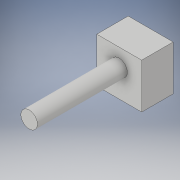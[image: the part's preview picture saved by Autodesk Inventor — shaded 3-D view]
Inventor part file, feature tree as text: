
AUTODESK INVENTOR PART (.ipt)
format: ipt  version: 2019 (Build 230136000, 136)  size: 99,328 bytes
history: native  units: in
note: dims shown in document units (in); Inventor stores cm internally (conversion verified against a paired STEP export)
features: extrude x2, sketch x2
ambient origin geometry x8: Origin, YZ Plane, XZ Plane, XY Plane, X Axis, Y Axis, Z Axis, Center Point
bodies: Body1 (feature_tree)
feature tree (4):
  extrude  "Extrusion2"  Depth=1.0in
  extrude  "Extrusion3"  Depth=2.0in TaperAngle=0.0deg
  sketch  "Sketch3"  dims[d2=1.0in d3=1.0in]
  sketch  "Sketch4"  dims[d4=0.7in d5=0.0in d6=2.0in d7=0.0in]
